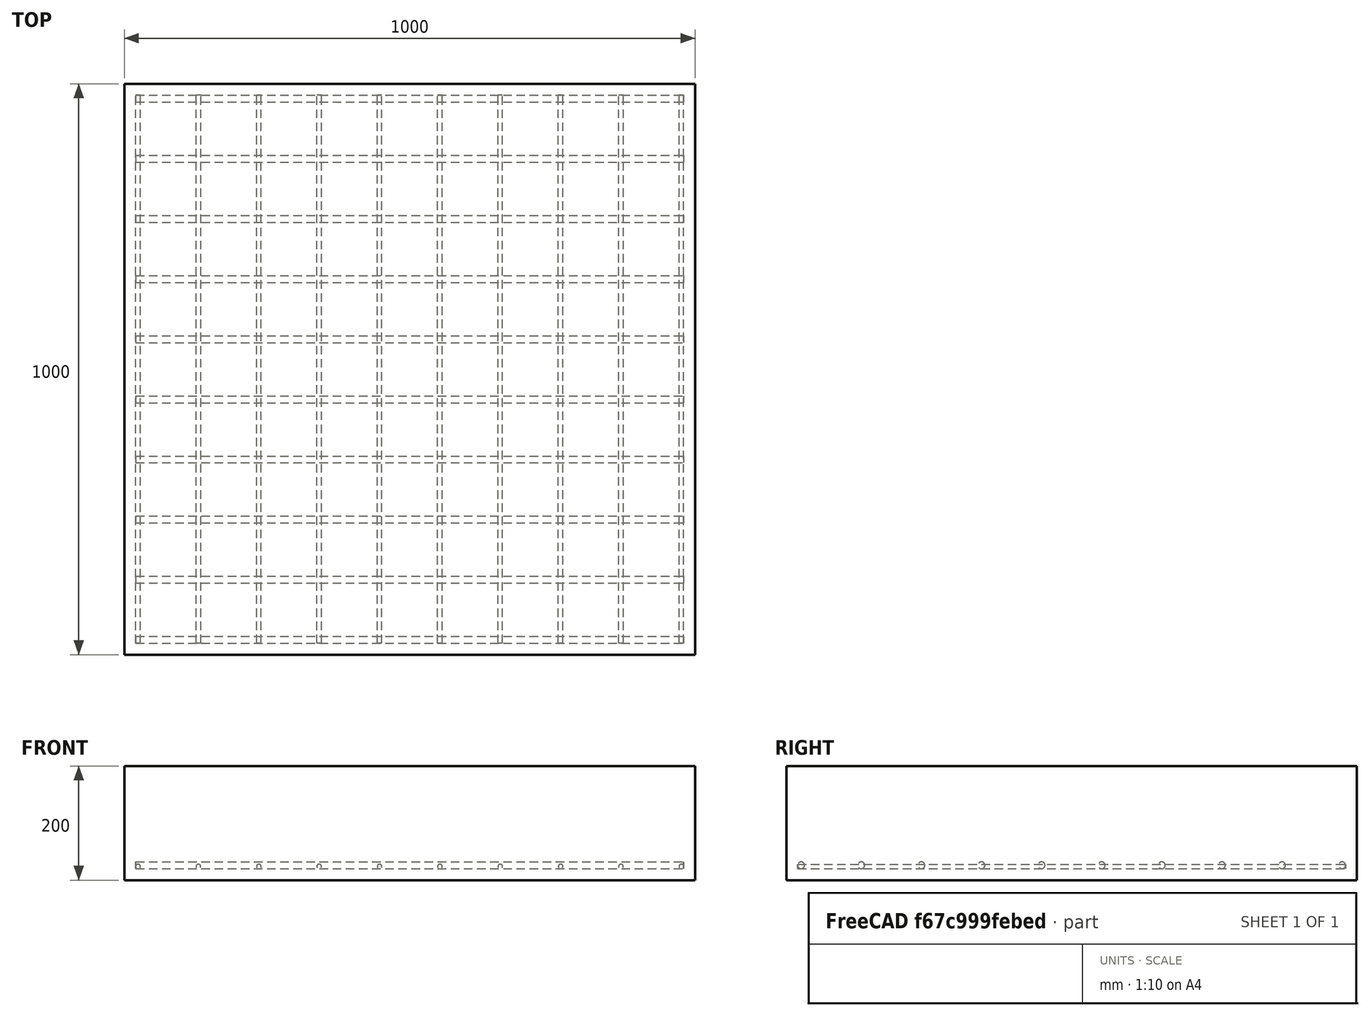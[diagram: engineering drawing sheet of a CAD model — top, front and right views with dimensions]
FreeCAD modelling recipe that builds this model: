
FCSTD DOCUMENT  (FreeCAD 0.21R33771 (Git))
Label: Slab Reinforcement
License: All rights reserved
objects: Part::FeaturePython×3, Sketcher::SketchObject×2, Part::Part2DObjectPython×1
note: 6 computed .brp shape members not serialized (recipe doc carries the construction recipe); baked Part::Feature solids carry a one-line shape summary decoded from their .brp

FEATURE [Part::Part2DObjectPython] Rectangle  # Draft 2D object (typed FeaturePython)
  Area = 1e+06
  ChamferSize = 0
  Columns = 1
  FilletRadius = 0
  Height = 1000
  Length = 1000
  MakeFace = true
  Placement = pos=(4000,-1000,0) rot=(0,0,1;0rad)
  Rows = 1
FEATURE [Part::FeaturePython] Structure  label="Slab"  # Arch/BIM 118 (typed FeaturePython)
  Base = -> Rectangle
  BaseMirror = false
  BaseOffsetX = 0
  BaseOffsetY = 0
  BasePerpendicularToTool = false
  BaseRotation = 0
  ComputedLength = 200
  FaceMaker = 0
  Height = 200
  HorizontalArea = 1e+06
  IfcData = attributes={"GlobalId": {"name": "GlobalId", "type": "IfcGloballyUniqueId", "is_enum": false, "enum_values": []}, "Description": {"... (+453 chars omitted),+1 more (map truncated)
  IfcType = 118
  Length = 1000
  MoveBase = false
  MoveWithHost = false
  Nodes = (4) [(4000,-1000,0),(5000,-1000,0),(5000,0,0),(4000,0,0)]
  NodesOffset = 0
  Normal = (0,0,-1)
  PerimeterLength = 4000
  PredefinedType = 0
  ToolOffsetFirst = 0
  ToolOffsetLast = 0
  VerticalArea = 800000
  Width = 1000
FEATURE [Sketcher::SketchObject] Sketch
  FullyConstrained = false
  MapMode = 5
  Placement = pos=(0,-1000,0) rot=(1,0,0;1.5708rad)
  Support = -> [Structure]
  sketch-geometry (1):
    g0: LineSegment StartX=4020 StartY=-174 StartZ=0 EndX=4980 EndY=-174 EndZ=0
FEATURE [Part::FeaturePython] Rebar  label="StraightRebar"  # Arch/BIM 110 (typed FeaturePython)
  Amount = 10
  AmountCheck = true
  Base = -> Sketch
  Cover = 20
  CoverAlong = Bottom Side
  Diameter = 12
  Direction = (0,0,0)
  Distance = 0
  FrontCover = 20
  HorizontalArea = 0
  Host = -> Structure
  IfcType = 110
  LeftBottomCover = 20
  Length = 960
  Mark = StraightRebar
  MoveBase = false
  MoveWithHost = false
  OffsetEnd = 26
  OffsetStart = 26
  Orientation = Horizontal
  PerimeterLength = 0
  PlacementList = 10 placements: arithmetic series from (0,26,-5.77316e-15) step (0,105.333,-2.33887e-14) to (0,974,-2.16271e-13)
  RebarShape = 0
  RightTopCover = 20
  Rounding = 0
  Spacing = 105.333
  TotalLength = 9600
  TrueSpacing = 10
  VerticalArea = 0
FEATURE [Sketcher::SketchObject] Sketch001
  FullyConstrained = false
  MapMode = 5
  Placement = pos=(5000,0,0) rot=(0.57735,0.57735,0.57735;2.0944rad)
  Support = -> [Structure]
  sketch-geometry (1):
    g0: LineSegment StartX=-980 StartY=-176 StartZ=0 EndX=-20 EndY=-176 EndZ=0
FEATURE [Part::FeaturePython] Rebar001  label="StraightRebar001"  # Arch/BIM 110 (typed FeaturePython)
  Amount = 10
  AmountCheck = true
  Base = -> Sketch001
  Cover = 20
  CoverAlong = Bottom Side
  Diameter = 8
  Direction = (0,0,0)
  Distance = 0
  FrontCover = 20
  HorizontalArea = 0
  Host = -> Structure
  IfcType = 110
  LeftBottomCover = 20
  Length = 960
  Mark = StraightRebar001
  MoveBase = false
  MoveWithHost = false
  OffsetEnd = 24
  OffsetStart = 24
  Orientation = Horizontal
  PerimeterLength = 0
  PlacementList = 10 placements: arithmetic series from (-24,0,0) step (-105.778,0,0) to (-976,0,0)
  RebarShape = 0
  RightTopCover = 20
  Rounding = 0
  Spacing = 105.778
  TotalLength = 9600
  TrueSpacing = 10
  VerticalArea = 0
